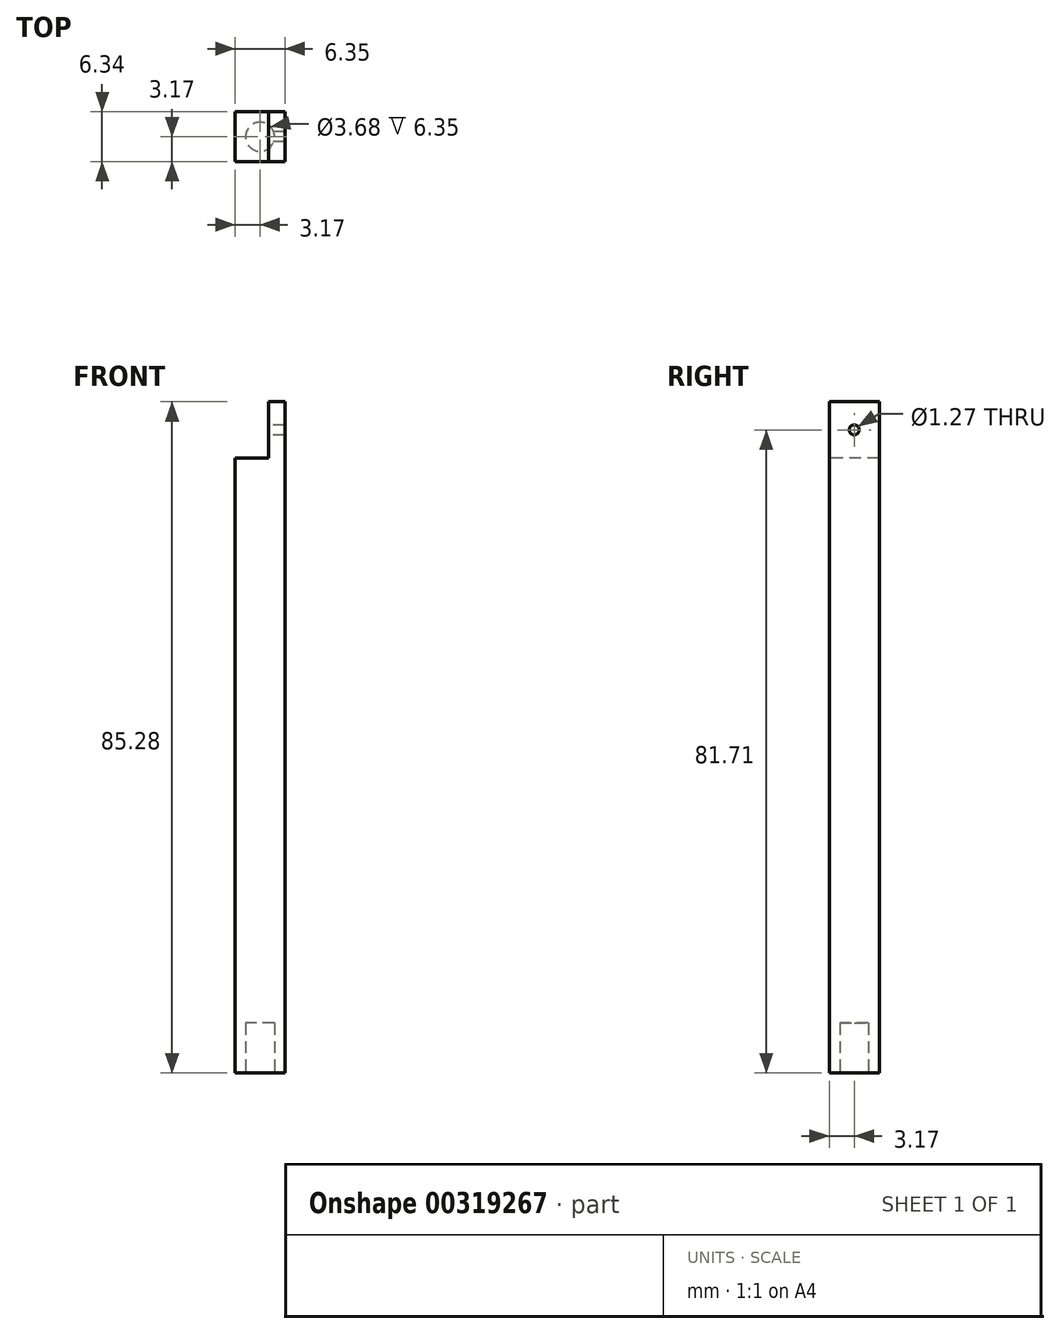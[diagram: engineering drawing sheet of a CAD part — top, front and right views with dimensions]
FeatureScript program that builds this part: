
annotation { "Feature Type Name" : "Feature", "Feature Type Description" : "" }
export const myFeature = defineFeature(function(context is Context, id is Id, definition is map)
    precondition{}
    {
        {
            var Q0;
            Q0=qCreatedBy(makeId("Top.planeOp"),FACE);
            var sketch = newSketch(context, id + "F0", { "sketchPlane" : qUnion([Q0])});
            skLineSegment(sketch, "E0.bottom", {"start": v(-3.17, 3.17) * mm, "end": v(3.18, 3.17) * mm});
            skLineSegment(sketch, "E0.top", {"start": v(-3.18, -3.18) * mm, "end": v(3.17, -3.18) * mm});
            skLineSegment(sketch, "E0.left", {"start": v(-3.18, 3.17) * mm, "end": v(-3.18, -3.18) * mm});
            skLineSegment(sketch, "E0.right", {"start": v(3.18, 3.17) * mm, "end": v(3.17, -3.18) * mm});
            skPoint(sketch, "E0.middle", {"position": v(0, 0) * mm});
            skCircle(sketch, "E1", {"center": v(0, 0) * mm, "radius": 1.84 * mm});
            skSolve(sketch);
        }
        {
            var Q0;
            Q0 = qSketchRegion(id + "F0", true);
            var Q1;
            Q1=makeQuery(id+"F0.imprint","IMPRINT",FACE,{"disambiguationData":[TD([[makeQuery(id+"F0.imprint","IMPRINT",EDGE,{"derivedFrom":sQuery(id+"F0.wireOp",EDGE,"E1")}),1.0]])]});
            extrude(context, id + "F1", {"entities" : qUnion([Q0, Q1]), "depth" : 78.14 * mm});
        }
        {
            var Q0;
            Q0=makeQuery(id+"F0.imprint","IMPRINT",FACE,{"disambiguationData":[TD([[makeQuery(id+"F0.imprint","IMPRINT",EDGE,{"derivedFrom":sQuery(id+"F0.wireOp",EDGE,"E1")}),1.0]])]});
            extrude(context, id + "F2", {"entities" : qUnion([Q0]), "operationType" : NewBodyOperationType.REMOVE, "depth" : 6.35 * mm});
        }
        {
            var Q0;
            Q0=qCreatedBy(makeId("Right.planeOp"),FACE);
            var sketch = newSketch(context, id + "F3", { "sketchPlane" : qUnion([Q0])});
            skLineSegment(sketch, "E2", {"start": v(0, 0) * mm, "end": v(0, 81.7) * mm, "construction": true});
            skLineSegment(sketch, "E3.bottom", {"start": v(3.18, 78.14) * mm, "end": v(-3.17, 78.14) * mm});
            skLineSegment(sketch, "E3.top", {"start": v(3.18, 85.28) * mm, "end": v(-3.17, 85.28) * mm});
            skLineSegment(sketch, "E3.left", {"start": v(3.18, 78.14) * mm, "end": v(3.18, 85.28) * mm});
            skLineSegment(sketch, "E3.right", {"start": v(-3.17, 78.14) * mm, "end": v(-3.17, 85.28) * mm});
            skPoint(sketch, "E3.middle", {"position": v(0, 81.7) * mm});
            skCircle(sketch, "E4", {"center": v(0, 81.7) * mm, "radius": 0.64 * mm});
            skSolve(sketch);
        }
        {
            var Q0;
            Q0 = qSketchRegion(id + "F3", true);
            extrude(context, id + "F4", {"entities" : qUnion([Q0]), "operationType" : NewBodyOperationType.ADD, "depth" : 3.17 * mm, "hasSecondDirection" : true, "secondDirectionOppositeDirection" : false, "secondDirectionDepth" : 1.06 * mm});
        }
    });
